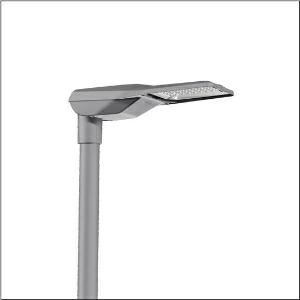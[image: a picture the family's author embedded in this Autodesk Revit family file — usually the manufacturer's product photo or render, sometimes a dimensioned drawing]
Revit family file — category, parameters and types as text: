
# Revit family: streetlight_sl_21_iq_mini___stw1_0a_5xe2e31d08jb_eadb
name_source: partatom
category: Lighting Fixtures
units: mm (PartAtom-declared; Revit-internal decimal feet)

## family parameters
Cut with Voids When Loaded = No
Host = Face
Light Source = No
Part Type = Normal
Room Calculation Point = No
Round Connector Dimension = Use Diameter
Shared = No

## types (1)
- --- (1 x LED, 10820 lm, 71.6 W, 3000K)
    Apparent Load = 72 VA
    CIE Flux Codes = 39 75 98 100 100
    Color Rendering = 70
    Color Temperature = 3000K
    Default Elevation = 1800 mm
    Description = Streetlight SL 21 iQ mini, mast luminaire, primary light control with lens, of PMMA, primary optical cover: cover, of toughened safety glass, transparent, light distribution: STW1.0a, light emission: direct distribution, primary light characteristic: asymmetric, installation type: post-top, side-entry, LED, High Power LED, rated luminous flux: 10.820lm, luminous efficacy: 151lm/W, light colour: 730, colour temperature: 3000K, control: Auto-Match, Temp-Guard, Lumen-Switch, Night-Set, Smart-Wire, Light-Fading, Desk-Remote (wireless, voltage-free reading and setting of iQ features in the workshop via application-optimized NFC function/RFID function), optimised constant luminous flux control (CLO 2.0), presetting dimming linear, mains connection: 220..240V, AC, 50/60Hz, start of lifetime: 72W, end of service life: 75W, reduction: 33W, luminaire housing, of diecast aluminium, powder-coated, Siteco® metallic grey (DB 702S), corrosivity category C5 mid according to DIN EN ISO 12944, please order mast flange separately, inclination adjustable: 0°, 5°, 10°, 15°, sealing non-destructively replaceable, multi-level sealing system, length: 628mm, width: 235mm, height: 110mm, mast flange for spigot size: 42mm (side-entry): 5XC10008XM4, 60/48mm (side-entry/post-top): 5XC10108XM2, 76/60mm (side-entry/post-top): 5XC10108XM1, protection rating (complete): IP66, insulation class (complete): insulation class II (safety insulation), certification: CE, ENEC, ENEC+, VDE, impact resistance: IK09, permissible operating ambient temperature for outdoor applications: -40..+50°C, standard-compliant lighting for roads and squares, packaging unit: 1 piece

Light Distribution: STW1.0a
    Height = 110 mm
    Lamp = 1 x LED
    Lamp Light Flux = 10820 lm
    Lamp Power = 71.6 W
    Lamp count = 1
    Length = 625 mm
    Luminous efficacy = 151 lm/W
    Manufacturer = Siteco
    ModVariant = No
    Model = 5XE2E31D08JB
    Number of Poles = 1
    OnlyDefault = Yes
    Power Factor = 1
    Product Name = Streetlight SL 21 iQ mini | STW1.0a
    Product group = mast luminaire | pylon top
    ProductGroupID = 6100
    Protection Class = Protection class II
    Protection Degree = IP 66
    RLX_Detail_Level = 1
    RLX_Emergency_Light_Flux = 0 lm
    RLX_Emergency_Type = 0
    RLX_Emergency_Type_DB = No
    RlxData = <blob elided: 92073 chars, md5=76b96e17>
    Socket = socket
    Standby Power = 0 W
    System Light Flux = 10820 lm
    System Power = 72 W
    Type Comments = factory setting: luminous flux: 100 % | dim-lin: 254 | 746 mA
    Type Image = l_1003519.jpg
    URL = http://relux.com
    VarID = @adj_120819
    Voltage = 0 V
    Weight = 0.00 kg
    Width = 234 mm

## geometry (parser evidence)
native form markers: Blend x4, Sweep x12
no freeform markers — native parametric forms only
